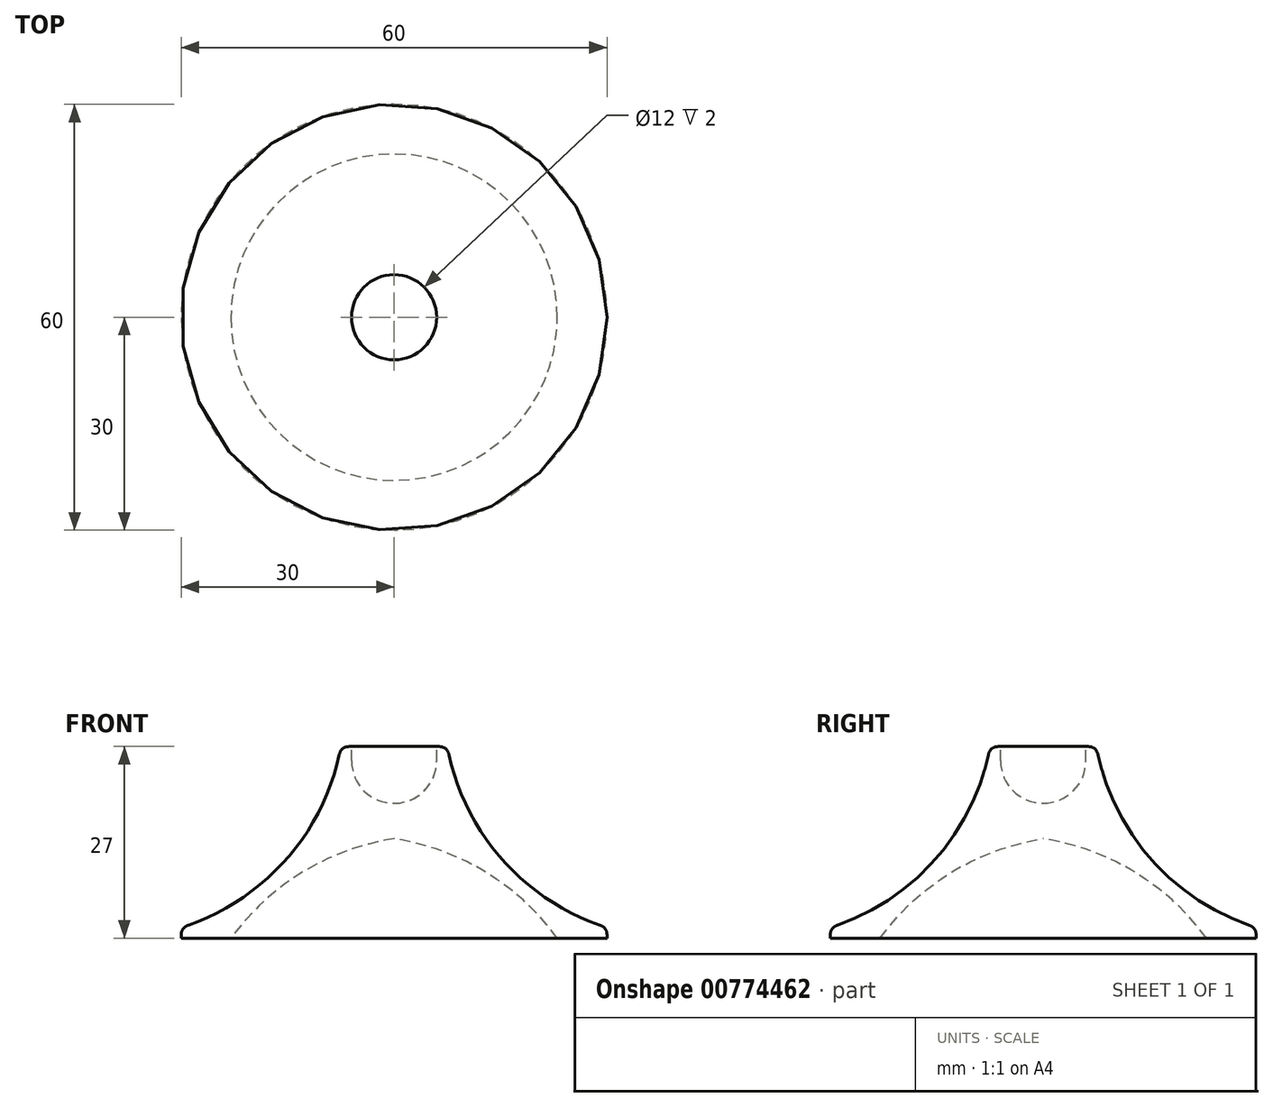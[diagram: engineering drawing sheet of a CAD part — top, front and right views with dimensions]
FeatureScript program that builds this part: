
annotation { "Feature Type Name" : "Feature", "Feature Type Description" : "" }
export const myFeature = defineFeature(function(context is Context, id is Id, definition is map)
    precondition{}
    {
        {
            var Q0;
            Q0=qCreatedBy(makeId("Front.planeOp"),FACE);
            var sketch = newSketch(context, id + "F0", { "sketchPlane" : qUnion([Q0])});
            skArc(sketch, "E0", {"start": v(0, 19) * mm, "mid": v(4.24, 20.76) * mm, "end": v(6, 25) * mm});
            skLineSegment(sketch, "E1", {"start": v(0, 19) * mm, "end": v(0, 14) * mm});
            skLineSegment(sketch, "E2", {"start": v(23, 0) * mm, "end": v(30, 0) * mm});
            skArc(sketch, "E3", {"start": v(7.5, 27) * mm, "mid": v(15.2, 11.1) * mm, "end": v(30, 1.5) * mm});
            skLineSegment(sketch, "E4", {"start": v(0, 19) * mm, "end": v(-8.69, 19) * mm, "construction": true});
            skLineSegment(sketch, "E5", {"start": v(30, 1.5) * mm, "end": v(30, 0) * mm});
            skArc(sketch, "E6", {"start": v(23, 0) * mm, "mid": v(12.9, 9.3) * mm, "end": v(0, 14) * mm});
            skLineSegment(sketch, "E7", {"start": v(0, 14) * mm, "end": v(-6.7, 14) * mm, "construction": true});
            skLineSegment(sketch, "E8", {"start": v(0, 25) * mm, "end": v(6, 25) * mm, "construction": true});
            skLineSegment(sketch, "E9", {"start": v(6, 25) * mm, "end": v(6, 27) * mm});
            skLineSegment(sketch, "E10", {"start": v(6, 27) * mm, "end": v(7.5, 27) * mm});
            skSolve(sketch);
        }
        {
            var Q0;
            Q0 = qSketchRegion(id + "F0", true);
            var Q1;
            Q1=sQuery(id+"F0.wireOp",EDGE,"E1");
            revolve(context, id + "F1", {"surfaceOperationType" : NewSurfaceOperationType.NEW, "entities" : qUnion([Q0]), "axis" : qUnion([Q1]), "revolveType" : RevolveType.FULL});
        }
        {
            var Q0;
            Q0=makeQuery(id+"F1.opRevolve","SWEPT_EDGE",EDGE,{"disambiguationData":[OSD([sQuery(id+"F0.wireOp",EDGE,"E3"),sQuery(id+"F0.wireOp",EDGE,"E10")])]});
            var Q1;
            Q1=makeQuery(id+"F1.opRevolve","SWEPT_EDGE",EDGE,{"disambiguationData":[OSD([sQuery(id+"F0.wireOp",EDGE,"E3"),sQuery(id+"F0.wireOp",EDGE,"E5")])]});
            fillet(context, id + "F2", {"entities" : qUnion([Q0, Q1]), "radius" : 1.5 * mm, "tangentPropagation" : true, "rho" : 0.5, "crossSection" : FilletCrossSection.CONIC, "allowEdgeOverflow" : false});
        }
    });
